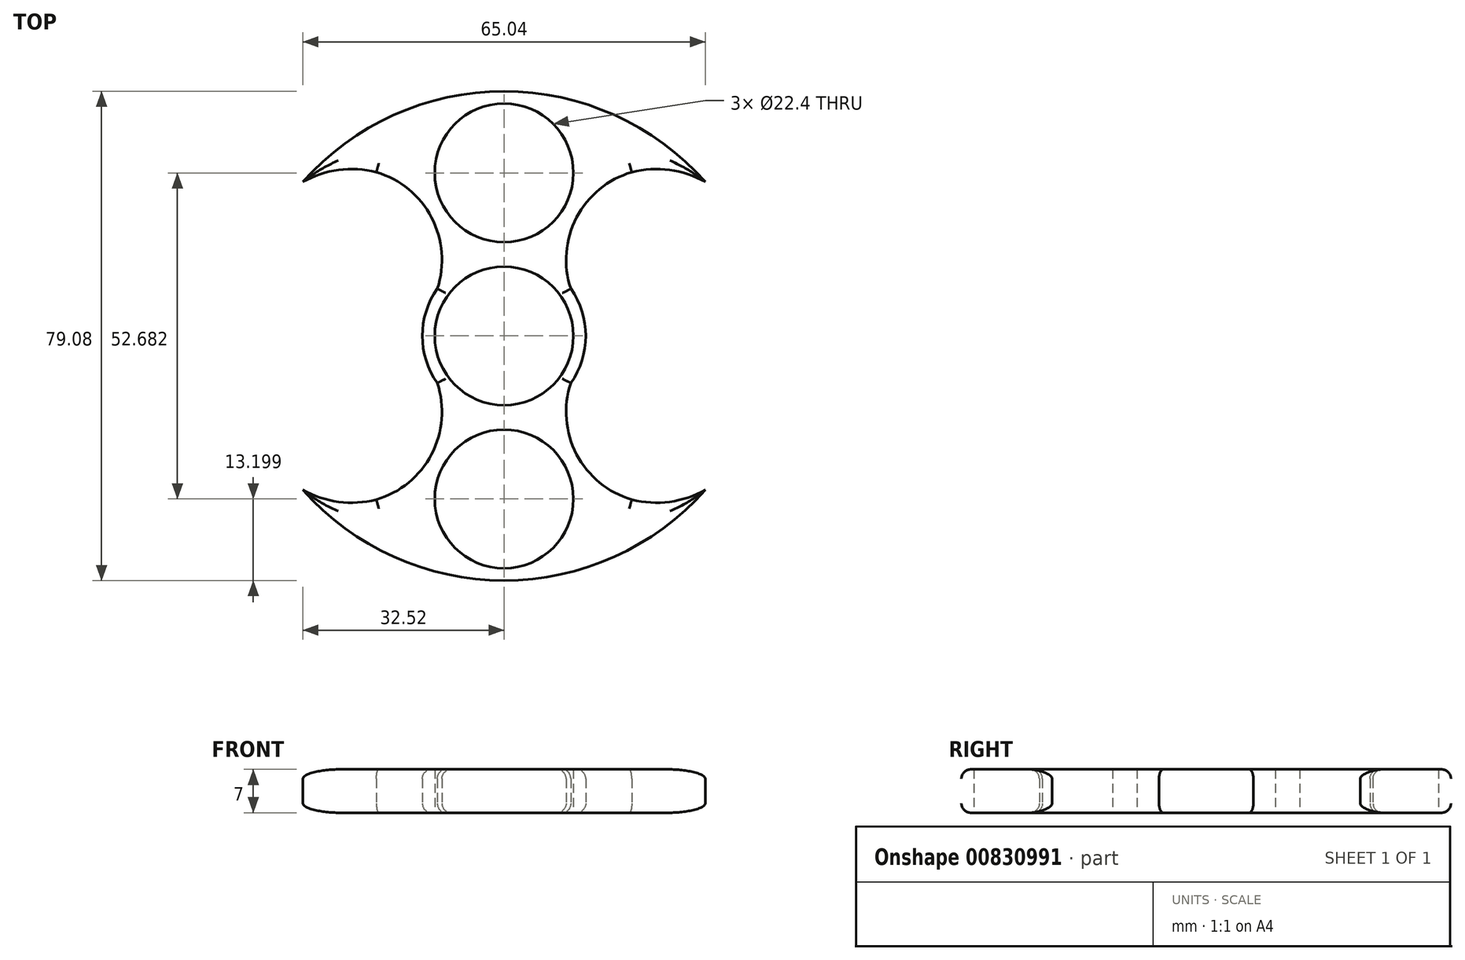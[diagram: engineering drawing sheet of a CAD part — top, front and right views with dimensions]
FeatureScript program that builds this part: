
annotation { "Feature Type Name" : "Feature", "Feature Type Description" : "" }
export const myFeature = defineFeature(function(context is Context, id is Id, definition is map)
    precondition{}
    {
        {
            var Q0;
            Q0=qCreatedBy(makeId("Top.planeOp"),FACE);
            var sketch = newSketch(context, id + "F0", { "sketchPlane" : qUnion([Q0])});
            skCircle(sketch, "E0", {"center": v(0, 0) * mm, "radius": 11.2 * mm});
            skArc(sketch, "E1", {"start": v(-10.78, 7.62) * mm, "mid": v(-13.2, 0) * mm, "end": v(-10.78, -7.62) * mm});
            skCircle(sketch, "E2", {"center": v(0, 26.34) * mm, "radius": 11.2 * mm});
            skCircle(sketch, "E3.1.0", {"center": v(0, -26.34) * mm, "radius": 11.2 * mm});
            skArc(sketch, "E3.1.1", {"start": v(-0.1, -39.54) * mm, "mid": v(0, -39.54) * mm, "end": v(0.1, -39.54) * mm});
            skArc(sketch, "E4", {"start": v(0, 39.54) * mm, "mid": v(-17.82, 35.68) * mm, "end": v(-32.52, 24.89) * mm});
            skArc(sketch, "E5", {"start": v(-20.63, 26.45) * mm, "mid": v(-26.72, 26.82) * mm, "end": v(-32.52, 24.89) * mm});
            skArc(sketch, "E6.MirrorCS", {"start": v(0, 39.54) * mm, "mid": v(17.82, 35.68) * mm, "end": v(32.52, 24.89) * mm});
            skArc(sketch, "E7.MirrorCS", {"start": v(20.63, 26.45) * mm, "mid": v(26.72, 26.82) * mm, "end": v(32.52, 24.89) * mm});
            skArc(sketch, "E8.MirrorCS", {"start": v(20.63, -26.45) * mm, "mid": v(26.72, -26.82) * mm, "end": v(32.52, -24.89) * mm});
            skArc(sketch, "E9.MirrorCS", {"start": v(-20.63, -26.45) * mm, "mid": v(-26.72, -26.82) * mm, "end": v(-32.52, -24.89) * mm});
            skArc(sketch, "E10.MirrorCS", {"start": v(0, -39.54) * mm, "mid": v(-17.82, -35.68) * mm, "end": v(-32.52, -24.89) * mm});
            skArc(sketch, "E11.MirrorCS", {"start": v(0, -39.54) * mm, "mid": v(17.82, -35.68) * mm, "end": v(32.52, -24.89) * mm});
            skArc(sketch, "E12", {"start": v(20.63, 26.45) * mm, "mid": v(11.71, 19.12) * mm, "end": v(10.78, 7.62) * mm});
            skArc(sketch, "E13.MirrorCS", {"start": v(-20.63, 26.45) * mm, "mid": v(-11.71, 19.12) * mm, "end": v(-10.78, 7.62) * mm});
            skArc(sketch, "E14.MirrorCS", {"start": v(-20.63, -26.45) * mm, "mid": v(-11.71, -19.12) * mm, "end": v(-10.78, -7.62) * mm});
            skArc(sketch, "E15.MirrorCS", {"start": v(20.63, -26.45) * mm, "mid": v(11.71, -19.12) * mm, "end": v(10.78, -7.62) * mm});
            skPoint(sketch, "E16.orphan", {"position": v(-12.02, 20.88) * mm});
            skPoint(sketch, "E17.orphan", {"position": v(-32.52, 24.89) * mm});
            skArc(sketch, "E18.trimOffspring", {"start": v(0.1, 39.54) * mm, "mid": v(0, 39.54) * mm, "end": v(-0.1, 39.54) * mm});
            skPoint(sketch, "E19.orphan", {"position": v(12.02, 20.88) * mm});
            skPoint(sketch, "E20.MirrorCS.start.orphan", {"position": v(-10.88, 18.87) * mm});
            skPoint(sketch, "E21.start.orphan", {"position": v(10.88, 18.87) * mm});
            skArc(sketch, "E22.trimOffspring", {"start": v(10.78, -7.62) * mm, "mid": v(13.2, 0) * mm, "end": v(10.78, 7.62) * mm});
            skPoint(sketch, "E23.MirrorCS.start.orphan", {"position": v(10.88, -18.87) * mm});
            skPoint(sketch, "E24.MirrorCS.start.orphan", {"position": v(-10.88, -18.87) * mm});
            skPoint(sketch, "E25.orphan", {"position": v(-12.02, -20.88) * mm});
            skPoint(sketch, "E26.orphan", {"position": v(12.02, -20.88) * mm});
            skPoint(sketch, "E27.orphan", {"position": v(32.52, -24.89) * mm});
            skPoint(sketch, "E28.orphan", {"position": v(-32.52, -24.89) * mm});
            skSolve(sketch);
        }
        {
            var Q0;
            Q0=makeQuery(id+"F0.imprint","IMPRINT",FACE,{"disambiguationData":[TD([[makeQuery(id+"F0.imprint","IMPRINT",EDGE,{"derivedFrom":sQuery(id+"F0.wireOp",EDGE,"E0")}),-1.0]])]});
            extrude(context, id + "F1", {"entities" : qUnion([Q0]), "depth" : 7 * mm, "offsetDistance" : 25 * mm});
        }
        {
            var Q0;
            Q0=makeQuery(id+"F1.opExtrude","CAP_EDGE",EDGE,{"disambiguationData":[OSD([sQuery(id+"F0.wireOp",EDGE,"E15.MirrorCS")])],"isStart":false});
            var Q1;
            Q1=makeQuery(id+"F1.opExtrude","CAP_EDGE",EDGE,{"disambiguationData":[OSD([sQuery(id+"F0.wireOp",EDGE,"E8.MirrorCS")])],"isStart":false});
            var Q2;
            Q2=makeQuery(id+"F1.opExtrude","CAP_EDGE",EDGE,{"disambiguationData":[OSD([sQuery(id+"F0.wireOp",EDGE,"E11.MirrorCS")])],"isStart":false});
            var Q3;
            Q3=makeQuery(id+"F1.opExtrude","CAP_EDGE",EDGE,{"disambiguationData":[OSD([sQuery(id+"F0.wireOp",EDGE,"E10.MirrorCS")])],"isStart":false});
            var Q4;
            Q4=makeQuery(id+"F1.opExtrude","CAP_EDGE",EDGE,{"disambiguationData":[OSD([sQuery(id+"F0.wireOp",EDGE,"E9.MirrorCS")])],"isStart":false});
            var Q5;
            Q5=makeQuery(id+"F1.opExtrude","CAP_EDGE",EDGE,{"disambiguationData":[OSD([sQuery(id+"F0.wireOp",EDGE,"E14.MirrorCS")])],"isStart":false});
            var Q6;
            Q6=makeQuery(id+"F1.opExtrude","CAP_EDGE",EDGE,{"disambiguationData":[OSD([sQuery(id+"F0.wireOp",EDGE,"E1")])],"isStart":false});
            var Q7;
            Q7=makeQuery(id+"F1.opExtrude","CAP_EDGE",EDGE,{"disambiguationData":[OSD([sQuery(id+"F0.wireOp",EDGE,"E13.MirrorCS")])],"isStart":false});
            var Q8;
            Q8=makeQuery(id+"F1.opExtrude","CAP_EDGE",EDGE,{"disambiguationData":[OSD([sQuery(id+"F0.wireOp",EDGE,"E5")])],"isStart":false});
            var Q9;
            Q9=makeQuery(id+"F1.opExtrude","CAP_EDGE",EDGE,{"disambiguationData":[OSD([sQuery(id+"F0.wireOp",EDGE,"E6.MirrorCS")])],"isStart":false});
            var Q10;
            Q10=makeQuery(id+"F1.opExtrude","CAP_EDGE",EDGE,{"disambiguationData":[OSD([sQuery(id+"F0.wireOp",EDGE,"E4")])],"isStart":false});
            var Q11;
            Q11=makeQuery(id+"F1.opExtrude","CAP_EDGE",EDGE,{"disambiguationData":[OSD([sQuery(id+"F0.wireOp",EDGE,"E7.MirrorCS")])],"isStart":false});
            var Q12;
            Q12=makeQuery(id+"F1.opExtrude","CAP_EDGE",EDGE,{"disambiguationData":[OSD([sQuery(id+"F0.wireOp",EDGE,"E12")])],"isStart":false});
            var Q13;
            Q13=makeQuery(id+"F1.opExtrude","CAP_EDGE",EDGE,{"disambiguationData":[OSD([sQuery(id+"F0.wireOp",EDGE,"E22.trimOffspring")])],"isStart":false});
            fillet(context, id + "F2", {"entities" : qUnion([Q0, Q1, Q2, Q3, Q4, Q5, Q6, Q7, Q8, Q9, Q10, Q11, Q12, Q13]), "radius" : 1.5 * mm, "tangentPropagation" : true, "allowEdgeOverflow" : false});
        }
        {
            var Q0;
            Q0=makeQuery(id+"F1.opExtrude","CAP_EDGE",EDGE,{"disambiguationData":[OSD([sQuery(id+"F0.wireOp",EDGE,"E4")])],"isStart":true});
            var Q1;
            Q1=makeQuery(id+"F1.opExtrude","CAP_EDGE",EDGE,{"disambiguationData":[OSD([sQuery(id+"F0.wireOp",EDGE,"E6.MirrorCS")])],"isStart":true});
            var Q2;
            Q2=makeQuery(id+"F1.opExtrude","CAP_EDGE",EDGE,{"disambiguationData":[OSD([sQuery(id+"F0.wireOp",EDGE,"E12")])],"isStart":true});
            var Q3;
            Q3=makeQuery(id+"F1.opExtrude","CAP_EDGE",EDGE,{"disambiguationData":[OSD([sQuery(id+"F0.wireOp",EDGE,"E7.MirrorCS")])],"isStart":true});
            var Q4;
            Q4=makeQuery(id+"F1.opExtrude","CAP_EDGE",EDGE,{"disambiguationData":[OSD([sQuery(id+"F0.wireOp",EDGE,"E22.trimOffspring")])],"isStart":true});
            var Q5;
            Q5=makeQuery(id+"F1.opExtrude","CAP_EDGE",EDGE,{"disambiguationData":[OSD([sQuery(id+"F0.wireOp",EDGE,"E15.MirrorCS")])],"isStart":true});
            var Q6;
            Q6=makeQuery(id+"F1.opExtrude","CAP_EDGE",EDGE,{"disambiguationData":[OSD([sQuery(id+"F0.wireOp",EDGE,"E8.MirrorCS")])],"isStart":true});
            var Q7;
            Q7=makeQuery(id+"F1.opExtrude","CAP_EDGE",EDGE,{"disambiguationData":[OSD([sQuery(id+"F0.wireOp",EDGE,"E10.MirrorCS")])],"isStart":true});
            var Q8;
            Q8=makeQuery(id+"F1.opExtrude","CAP_EDGE",EDGE,{"disambiguationData":[OSD([sQuery(id+"F0.wireOp",EDGE,"E14.MirrorCS")])],"isStart":true});
            var Q9;
            Q9=makeQuery(id+"F1.opExtrude","CAP_EDGE",EDGE,{"disambiguationData":[OSD([sQuery(id+"F0.wireOp",EDGE,"E9.MirrorCS")])],"isStart":true});
            var Q10;
            Q10=makeQuery(id+"F1.opExtrude","CAP_EDGE",EDGE,{"disambiguationData":[OSD([sQuery(id+"F0.wireOp",EDGE,"E1")])],"isStart":true});
            var Q11;
            Q11=makeQuery(id+"F1.opExtrude","CAP_EDGE",EDGE,{"disambiguationData":[OSD([sQuery(id+"F0.wireOp",EDGE,"E13.MirrorCS")])],"isStart":true});
            var Q12;
            Q12=makeQuery(id+"F1.opExtrude","CAP_EDGE",EDGE,{"disambiguationData":[OSD([sQuery(id+"F0.wireOp",EDGE,"E5")])],"isStart":true});
            fillet(context, id + "F3", {"entities" : qUnion([Q0, Q1, Q2, Q3, Q4, Q5, Q6, Q7, Q8, Q9, Q10, Q11, Q12]), "radius" : 1.5 * mm, "tangentPropagation" : true, "allowEdgeOverflow" : false});
        }
    });
